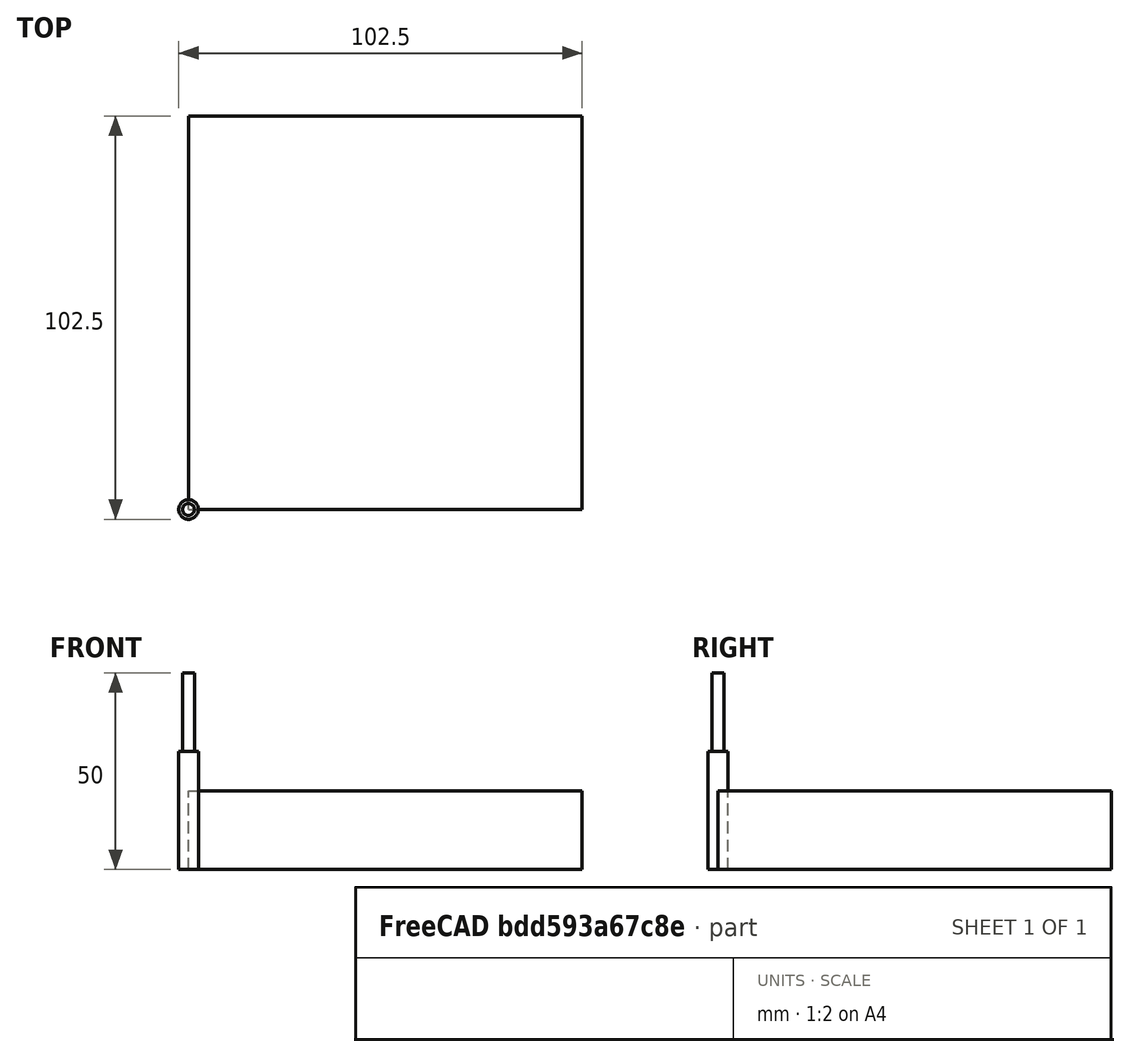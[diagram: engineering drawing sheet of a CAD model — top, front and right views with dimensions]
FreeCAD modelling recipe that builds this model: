
FCSTD DOCUMENT  (FreeCAD 0.19R23756 (Git))
Label: 203 - CNC MACHINING
License: Creative Commons Attribution-NonCommercial
LicenseURL: http://creativecommons.org/licenses/by-nc/4.0/
objects: Path::FeaturePython×5, Part::FeaturePython×3, Mesh::FeaturePython×3, Part::Box×2, App::DocumentObjectGroup×2, Part::Cylinder×1, Part::Fillet×1, Part::Cut×1, Part::MultiFuse×1, App::FeaturePython×1, Path::FeatureCompoundPython×1
note: 12 computed .brp shape members not serialized (recipe doc carries the construction recipe); baked Part::Feature solids carry a one-line shape summary decoded from their .brp

FEATURE [Part::Box] Box  label="Cube"
  AttacherType = Attacher::AttachEngine3D
  Height = 10
  Length = 100
  Width = 100
FEATURE [Part::Box] Box001  label="Cube001"
  AttacherType = Attacher::AttachEngine3D
  Height = 10
  Length = 60
  Placement = pos=(20,20,10) rot=(0,0,1;0rad)
  Width = 60
FEATURE [Part::Cylinder] Cylinder
  Angle = 360
  AttacherType = Attacher::AttachEngine3D
  Height = 10
  Placement = pos=(50,50,10) rot=(0,0,1;0rad)
  Radius = 25
FEATURE [Part::Fillet] Fillet
  Base = -> Box001
  Edges = 2 edges r=15: [Edge1,Edge3]
FEATURE [Part::Cut] Cut
  Base = -> Fillet
  Tool = -> Cylinder
FEATURE [Part::MultiFuse] Fusion
  Shapes = -> [Cut,Box]
FEATURE [App::FeaturePython] SetupSheet  # Path/CAM operation (typed FeaturePython)
  ClearanceHeightExpression = OpStockZMax+SetupSheet.ClearanceHeightOffset
  ClearanceHeightOffset = 5
  CoolantMode = 0
  CoolantModes = None | Flood | Mist
  FinalDepthExpression = OpFinalDepth
  HorizRapid = 0
  SafeHeightExpression = OpStockZMax+SetupSheet.SafeHeightOffset
  SafeHeightOffset = 3
  StartDepthExpression = OpStartDepth
  StepDownExpression = OpToolDiameter
  VertRapid = 0
FEATURE [Part::FeaturePython] Clone  label="Model-Fusion"  # Draft clone (typed FeaturePython)
  AttacherType = Attacher::AttachEngine3D
  Fuse = false
  Objects = -> [Fusion]
  PathResource = Model
  Scale = (1,1,1)
FEATURE [App::DocumentObjectGroup] Model
  Group = -> [Clone]
FEATURE [Part::FeaturePython] Stock  # WARN: FeaturePython — macro-defined, semantics opaque (R4)
  Height = 20
  Length = 100
  StockType = CreateBox
  Width = 100
FEATURE [Part::FeaturePython] ToolBit001  label="5mm Endmill"  # Path/CAM toolbit (typed FeaturePython)
  BitShape = <path>
  CuttingEdgeHeight = 30
  Diameter = 5
  File = <path>
  Length = 50
  ShankDiameter = 3
  ShapeName = endmill
FEATURE [Path::FeaturePython] TC__5mm_Endmill  label="TC: 5mm Endmill"  # Path/CAM operation (typed FeaturePython)
  HorizFeed = 5
  HorizRapid = 0
  SpindleDir = 0
  SpindleSpeed = 0
  Tool = -> ToolBit001
  ToolNumber = 1
  VertFeed = 5
  VertRapid = 0
  expr: VertRapid = SetupSheet.VertRapid
  expr: HorizRapid = SetupSheet.HorizRapid
FEATURE [App::DocumentObjectGroup] Tools
  Group = -> [TC__5mm_Endmill]
FEATURE [Path::FeaturePython] Profile  # Path/CAM operation (typed FeaturePython)
  Active = true
  AreaParams:
    Tolerance = 1e-07
    FitArcs = True
    Simplify = False
    CleanDistance = 0.0
    Accuracy = 0.01
    Unit = 1.0
    MinArcPoints = 4
    MaxArcPoints = 100
    ClipperScale = 10000000.0
    Fill = 0
    Coplanar = 0
    Reorient = True
    Outline = False
    Explode = False
    OpenMode = 0
    Deflection = 0.01
    SubjectFill = 0
    ClipFill = 0
    Offset = 0.5
    ExtraPass = 0
    Stepover = 0.0
    LastStepover = 0.0
    JoinType = 0
    EndType = 0
    MiterLimit = 2.0
    RoundPrecision = 0.0
    PocketMode = 0
    ToolRadius = 1.0
    PocketExtraOffset = 0.0
    PocketStepover = 0.0
    PocketLastStepover = 0.0
    FromCenter = False
    Angle = 45.0
    AngleShift = 0.0
    Shift = 0.0
    Thicken = False
    SectionCount = -1
    Stepdown = 1.0
    SectionOffset = 0.0
    SectionTolerance = 1e-06
    SectionMode = 2
    Project = False
  AttemptInverseAngle = true
  Base = -> [Clone]
  ClearanceHeight = 25
  CoolantMode = None
  CycleTime = 00:03:20
  Direction = 0
  EnableRotation = 0
  ExpandProfile = 0
  ExpandProfileStepOver = 100
  FinalDepth = 10
  HandleMultipleFeatures = 1
  InverseAngle = false
  JoinType = 0
  LimitDepthToFace = true
  MiterLimit = 0.1
  OffsetExtra = -3
  OpFinalDepth = 10
  OpStartDepth = 20
  OpStockZMax = 20
  OpStockZMin = 0
  OpToolDiameter = 5
  PathParams = {'orientation': 1, 'feedrate': 5.0, 'feedrate_v': 5.0, 'verbose': True, 'resume_height': 23.0, 'retraction': 25.0, 'return_end': True, 'preamble': False}
  ReverseDirection = false
  SafeHeight = 23
  Side = 1
  StartDepth = 20
  StartPoint = (0,0,0)
  StepDown = 5
  ToolController = -> TC__5mm_Endmill
  UseComp = true
  UseStartPoint = false
  processCircles = false
  processHoles = false
  processPerimeter = true
  expr: StartDepth = OpStartDepth
  expr: FinalDepth = OpFinalDepth
  expr: StepDown = OpToolDiameter
  expr: SafeHeight = OpStockZMax + SetupSheet.SafeHeightOffset
  expr: ClearanceHeight = OpStockZMax + SetupSheet.ClearanceHeightOffset
FEATURE [Path::FeaturePython] Pocket_Shape  # Path/CAM operation (typed FeaturePython)
  Active = true
  AreaParams:
    Tolerance = 1e-07
    FitArcs = True
    Simplify = False
    CleanDistance = 0.0
    Accuracy = 0.01
    Unit = 1.0
    MinArcPoints = 4
    MaxArcPoints = 100
    ClipperScale = 10000000.0
    Fill = 0
    Coplanar = 0
    Reorient = True
    Outline = False
    Explode = False
    OpenMode = 0
    Deflection = 0.01
    SubjectFill = 0
    ClipFill = 0
    Offset = 0.0
    ExtraPass = 0
    Stepover = 0.0
    LastStepover = 0.0
    JoinType = 0
    EndType = 0
    MiterLimit = 2.0
    RoundPrecision = 0.0
    PocketMode = 4
    ToolRadius = 2.5
    PocketExtraOffset = 0.0
    PocketStepover = 5.0
    PocketLastStepover = 0.0
    FromCenter = True
    Angle = 45.0
    AngleShift = 0.0
    Shift = 0.0
    Thicken = False
    SectionCount = -1
    Stepdown = 1.0
    SectionOffset = 0.0
    SectionTolerance = 1e-06
    SectionMode = 2
    Project = False
  AttemptInverseAngle = true
  Base = -> [Clone]
  ClearanceHeight = 25
  CoolantMode = None
  CutMode = 0
  CycleTime = 00:14:24
  EnableRotation = 0
  ExtensionCorners = true
  ExtensionLengthDefault = 2.5
  ExtraOffset = 0
  FinalDepth = 10
  FinishDepth = 0
  InverseAngle = false
  KeepToolDown = false
  LimitDepthToFace = true
  MinTravel = false
  OffsetPattern = 3
  OpFinalDepth = 10
  OpStartDepth = 20
  OpStockZMax = 20
  OpStockZMin = 0
  OpToolDiameter = 5
  PathParams = {'orientation': 1, 'feedrate': 5.0, 'feedrate_v': 5.0, 'verbose': True, 'resume_height': 23.0, 'retraction': 25.0, 'return_end': True, 'preamble': False}
  ReverseDirection = false
  SafeHeight = 23
  StartAt = 0
  StartDepth = 20
  StartPoint = (0,0,0)
  StepDown = 5
  StepOver = 100
  ToolController = -> TC__5mm_Endmill
  UseOutline = false
  UseStartPoint = false
  ZigZagAngle = 45
  expr: StartDepth = OpStartDepth
  expr: FinalDepth = OpFinalDepth
  expr: StepDown = OpToolDiameter
  expr: SafeHeight = OpStockZMax + SetupSheet.SafeHeightOffset
  expr: ClearanceHeight = OpStockZMax + SetupSheet.ClearanceHeightOffset
  expr: ExtensionLengthDefault = OpToolDiameter / 2
FEATURE [Path::FeaturePython] Pocket_Shape001  # Path/CAM operation (typed FeaturePython)
  Active = true
  AreaParams:
    Tolerance = 1e-07
    FitArcs = True
    Simplify = False
    CleanDistance = 0.0
    Accuracy = 0.01
    Unit = 1.0
    MinArcPoints = 4
    MaxArcPoints = 100
    ClipperScale = 10000000.0
    Fill = 0
    Coplanar = 0
    Reorient = True
    Outline = False
    Explode = False
    OpenMode = 0
    Deflection = 0.01
    SubjectFill = 0
    ClipFill = 0
    Offset = 0.0
    ExtraPass = 0
    Stepover = 0.0
    LastStepover = 0.0
    JoinType = 0
    EndType = 0
    MiterLimit = 2.0
    RoundPrecision = 0.0
    PocketMode = 4
    ToolRadius = 2.5
    PocketExtraOffset = 0.0
    PocketStepover = 5.0
    PocketLastStepover = 0.0
    FromCenter = True
    Angle = 45.0
    AngleShift = 0.0
    Shift = 0.0
    Thicken = False
    SectionCount = -1
    Stepdown = 1.0
    SectionOffset = 0.0
    SectionTolerance = 1e-06
    SectionMode = 2
    Project = False
  AttemptInverseAngle = true
  Base = -> [Clone]
  ClearanceHeight = 25
  CoolantMode = None
  CutMode = 0
  CycleTime = 00:03:37
  EnableRotation = 0
  ExtensionCorners = true
  ExtensionLengthDefault = 2.5
  ExtraOffset = 0
  FinalDepth = 10
  FinishDepth = 0
  InverseAngle = false
  KeepToolDown = false
  LimitDepthToFace = true
  MinTravel = false
  OffsetPattern = 3
  OpFinalDepth = 10
  OpStartDepth = 20
  OpStockZMax = 20
  OpStockZMin = 0
  OpToolDiameter = 5
  PathParams = {'orientation': 1, 'feedrate': 5.0, 'feedrate_v': 5.0, 'verbose': True, 'resume_height': 23.0, 'retraction': 25.0, 'return_end': True, 'preamble': False}
  ReverseDirection = false
  SafeHeight = 23
  StartAt = 0
  StartDepth = 20
  StartPoint = (0,0,0)
  StepDown = 5
  StepOver = 100
  ToolController = -> TC__5mm_Endmill
  UseOutline = false
  UseStartPoint = false
  ZigZagAngle = 45
  expr: StartDepth = OpStartDepth
  expr: FinalDepth = OpFinalDepth
  expr: StepDown = OpToolDiameter
  expr: SafeHeight = OpStockZMax + SetupSheet.SafeHeightOffset
  expr: ClearanceHeight = OpStockZMax + SetupSheet.ClearanceHeightOffset
  expr: ExtensionLengthDefault = OpToolDiameter / 2
FEATURE [Path::FeatureCompoundPython] Operations  # Path/CAM operation (typed FeaturePython)
  Group = -> [Profile,Pocket_Shape,Pocket_Shape001]
  UsePlacements = false
FEATURE [Path::FeaturePython] Job  # Path/CAM operation (typed FeaturePython)
  CycleTime = 00:21:21
  Fixtures = G54
  GeometryTolerance = 0.01
  Model = -> Model
  Operations = -> Operations
  OrderOutputBy = 0
  PostProcessor = 1
  SetupSheet = -> SetupSheet
  SplitOutput = false
  Stock = -> Stock
  Tools = -> Tools
FEATURE [Mesh::FeaturePython] CutMaterial  # WARN: FeaturePython — macro-defined, semantics opaque (R4)
FEATURE [Mesh::FeaturePython] CutMaterial001  # WARN: FeaturePython — macro-defined, semantics opaque (R4)
FEATURE [Mesh::FeaturePython] CutMaterial002  # WARN: FeaturePython — macro-defined, semantics opaque (R4)
note: 2 file-system paths scrubbed to <path> (originals preserved in the JSON sidecar)
